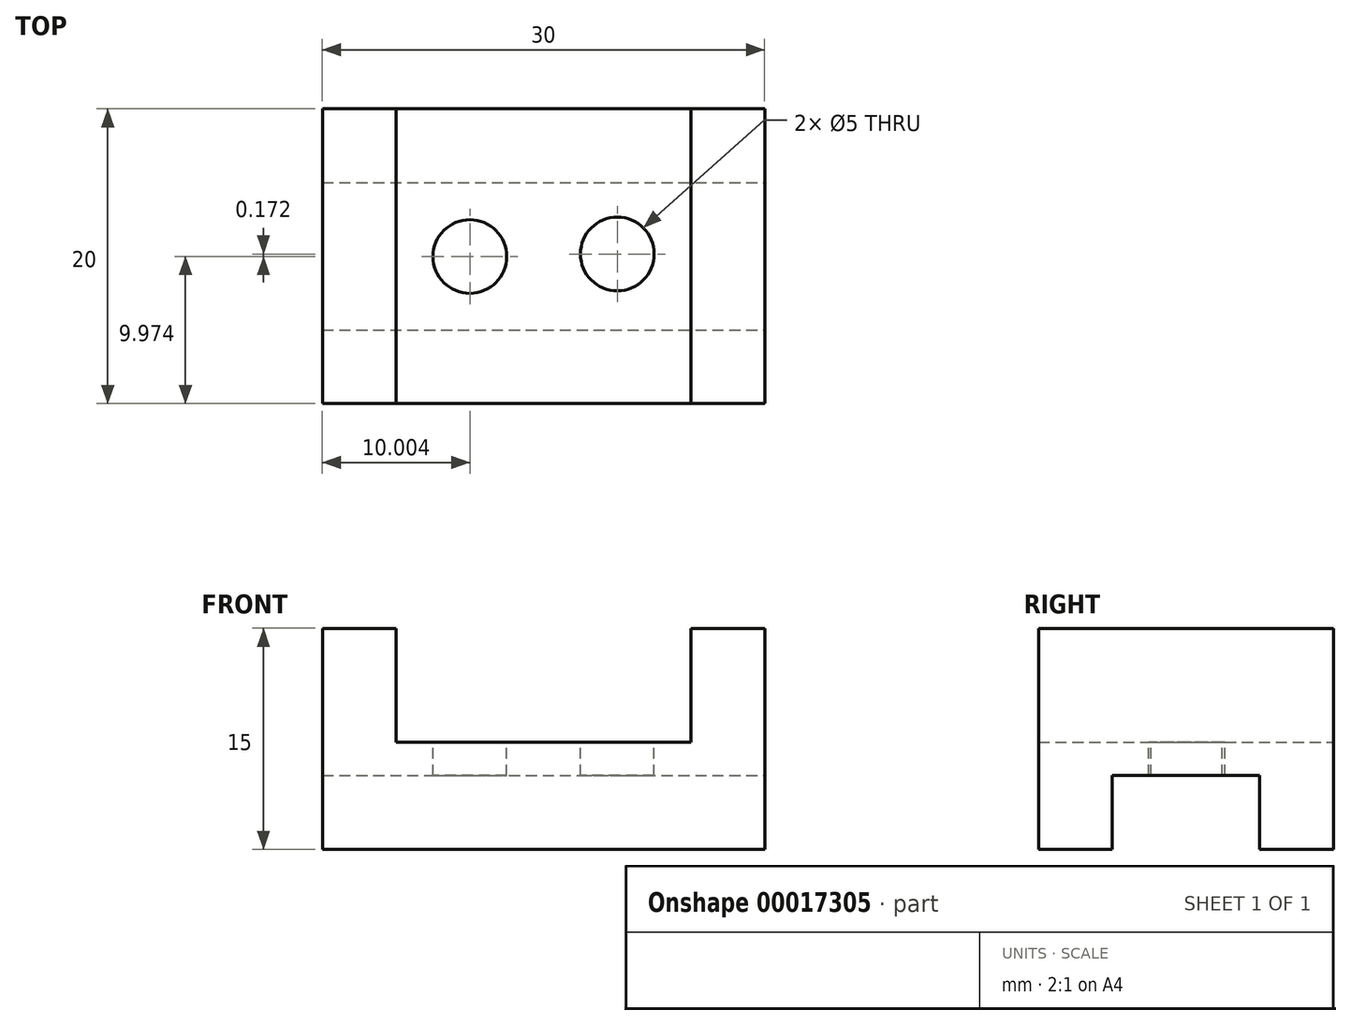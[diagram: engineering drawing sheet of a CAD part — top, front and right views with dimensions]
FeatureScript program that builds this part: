
annotation { "Feature Type Name" : "Feature", "Feature Type Description" : "" }
export const myFeature = defineFeature(function(context is Context, id is Id, definition is map)
    precondition{}
    {
        {
            var Q0;
            Q0=qCreatedBy(makeId("Front.planeOp"),FACE);
            var sketch = newSketch(context, id + "F0", { "sketchPlane" : qUnion([Q0])});
            skLineSegment(sketch, "E0", {"start": v(-12.68, 7.74) * mm, "end": v(-12.68, -7.26) * mm});
            skLineSegment(sketch, "E1", {"start": v(-12.68, -7.26) * mm, "end": v(17.32, -7.26) * mm});
            skLineSegment(sketch, "E2", {"start": v(17.32, -7.26) * mm, "end": v(17.32, 7.74) * mm});
            skLineSegment(sketch, "E3", {"start": v(17.32, 7.74) * mm, "end": v(12.32, 7.74) * mm});
            skLineSegment(sketch, "E4", {"start": v(12.32, 7.74) * mm, "end": v(12.32, 0) * mm});
            skLineSegment(sketch, "E5", {"start": v(12.32, 0) * mm, "end": v(-7.68, 0) * mm});
            skLineSegment(sketch, "E6", {"start": v(-7.68, 0) * mm, "end": v(-7.68, 7.74) * mm});
            skLineSegment(sketch, "E7", {"start": v(-7.68, 7.74) * mm, "end": v(-12.68, 7.74) * mm});
            skSolve(sketch);
        }
        {
            var Q0;
            Q0=makeQuery(id+"F0.imprint","IMPRINT",FACE,{"disambiguationData":[TD([[makeQuery(id+"F0.imprint","IMPRINT",EDGE,{"derivedFrom":sQuery(id+"F0.wireOp",EDGE,"E0")}),1.0]])]});
            extrude(context, id + "F1", {"entities" : qUnion([Q0]), "depth" : 20 * mm});
        }
        {
            var Q0;
            Q0=makeQuery(id+"F1.opExtrude","SWEPT_FACE",FACE,{"disambiguationData":[OSD([sQuery(id+"F0.wireOp",EDGE,"E5")])]});
            var sketch = newSketch(context, id + "F2", { "sketchPlane" : qUnion([Q0])});
            skCircle(sketch, "E8", {"center": v(-2.68, -10.03) * mm, "radius": 2.5 * mm});
            skCircle(sketch, "E9", {"center": v(7.33, -9.85) * mm, "radius": 2.5 * mm});
            skSolve(sketch);
        }
        {
            var Q0;
            Q0=makeQuery(id+"F2.imprint","IMPRINT",FACE,{"disambiguationData":[TD([[makeQuery(id+"F2.imprint","IMPRINT",EDGE,{"derivedFrom":sQuery(id+"F2.wireOp",EDGE,"E8")}),1.0]])]});
            var Q1;
            Q1=makeQuery(id+"F2.imprint","IMPRINT",FACE,{"disambiguationData":[TD([[makeQuery(id+"F2.imprint","IMPRINT",EDGE,{"derivedFrom":sQuery(id+"F2.wireOp",EDGE,"E9")}),1.0]])]});
            extrude(context, id + "F3", {"entities" : qUnion([Q0, Q1]), "operationType" : NewBodyOperationType.REMOVE, "oppositeDirection" : true, "depth" : 25 * mm});
        }
        {
            var Q0;
            Q0=makeQuery(id+"F1.opExtrude","SWEPT_FACE",FACE,{"disambiguationData":[OSD([sQuery(id+"F0.wireOp",EDGE,"E2")])]});
            var sketch = newSketch(context, id + "F4", { "sketchPlane" : qUnion([Q0])});
            skLineSegment(sketch, "E10.top", {"start": v(-5, -2.26) * mm, "end": v(-15, -2.26) * mm});
            skLineSegment(sketch, "E10.left", {"start": v(-5, -7.26) * mm, "end": v(-5, -2.26) * mm});
            skLineSegment(sketch, "E10.right", {"start": v(-15, -7.26) * mm, "end": v(-15, -2.26) * mm});
            skLineSegment(sketch, "E11", {"start": v(-5, -7.26) * mm, "end": v(0, -7.26) * mm});
            skLineSegment(sketch, "E12", {"start": v(-15, -7.26) * mm, "end": v(-20, -7.26) * mm});
            skSolve(sketch);
        }
        {
            var Q0;
            Q0=makeQuery(id+"F4.imprint","IMPRINT",FACE,{"disambiguationData":[TD([[makeQuery(id+"F4.imprint","IMPRINT",EDGE,{"derivedFrom":sQuery(id+"F4.wireOp",EDGE,"E10.top")}),1.0]])]});
            extrude(context, id + "F5", {"entities" : qUnion([Q0]), "operationType" : NewBodyOperationType.REMOVE, "oppositeDirection" : true, "depth" : 30 * mm});
        }
    });
